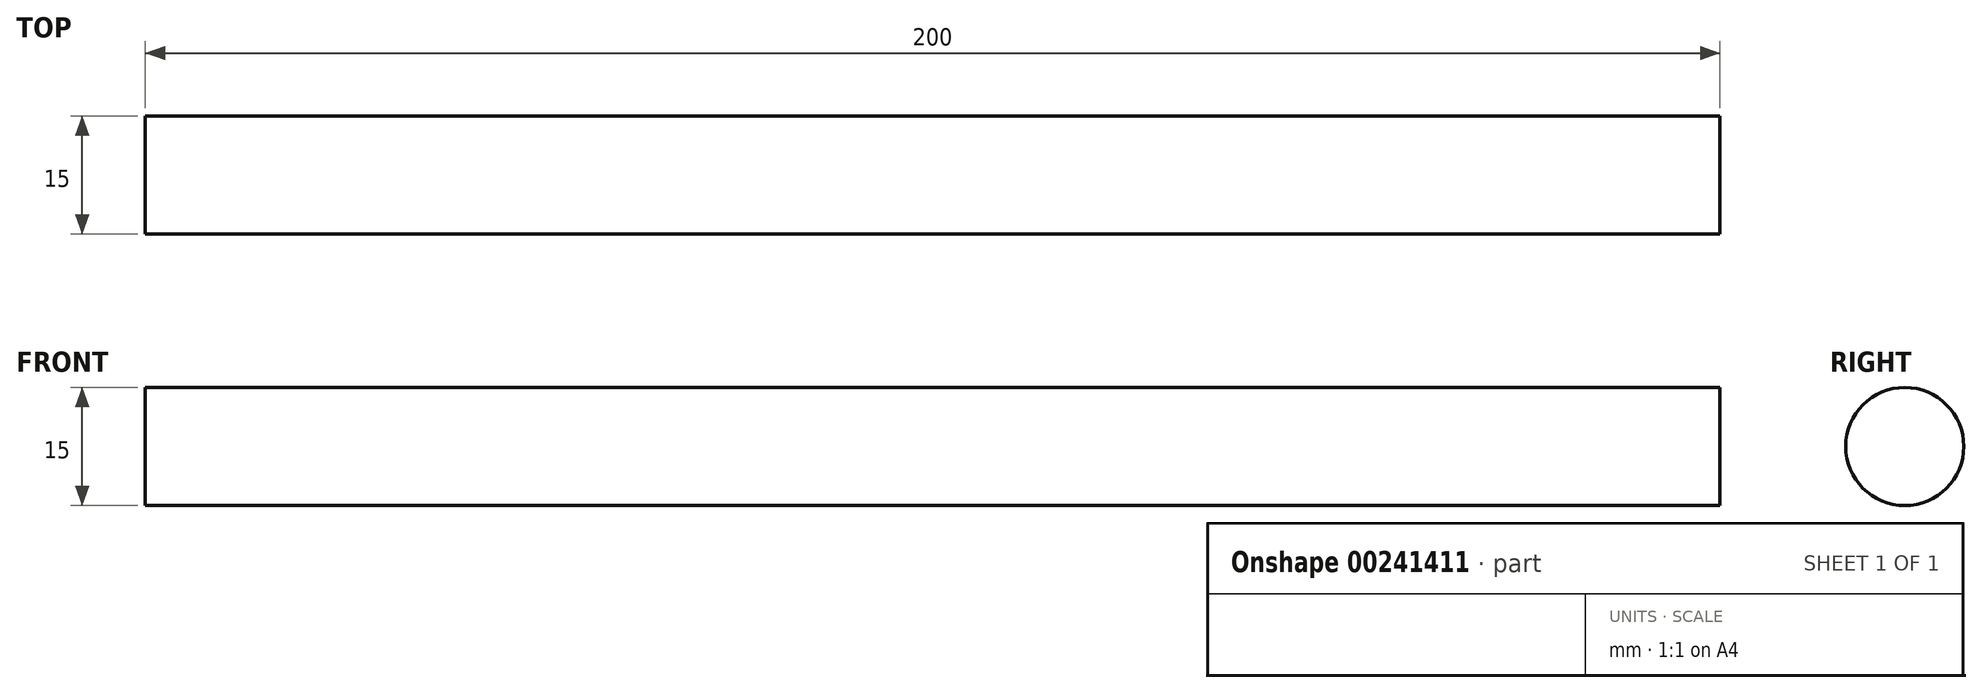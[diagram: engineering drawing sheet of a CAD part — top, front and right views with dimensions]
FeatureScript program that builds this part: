
annotation { "Feature Type Name" : "Feature", "Feature Type Description" : "" }
export const myFeature = defineFeature(function(context is Context, id is Id, definition is map)
    precondition{}
    {
        {
            var Q0;
            Q0=qCreatedBy(makeId("Right.planeOp"),FACE);
            var sketch = newSketch(context, id + "F0", { "sketchPlane" : qUnion([Q0])});
            skCircle(sketch, "E0", {"center": v(0, 0) * mm, "radius": 7.5 * mm});
            skSolve(sketch);
        }
        {
            var Q0;
            Q0 = qSketchRegion(id + "F0", true);
            extrude(context, id + "F1", {"entities" : qUnion([Q0]), "depth" : 200 * mm});
        }
    });
